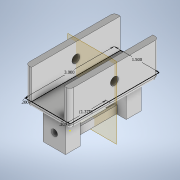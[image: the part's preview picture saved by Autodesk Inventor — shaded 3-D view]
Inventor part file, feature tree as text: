
AUTODESK INVENTOR PART (.ipt)
format: ipt  version: 2020 (Build 240168000, 168)  size: 665,600 bytes
history: native  units: in
note: dims shown in document units (in); Inventor stores cm internally (conversion verified against a paired STEP export)
features: sketch x8, extrude x5, hole x4, fillet x1, plane x1, mirror x1
ambient origin geometry x8: Origin, YZ Plane, XZ Plane, XY Plane, X Axis, Y Axis, Z Axis, Center Point
bodies: Solid1 (feature_tree)
feature tree (20):
  sketch  "Sketch1"  dims[d0=1.5in d1=3.0in]
  extrude  "Extrusion1"  Depth=3.0in
  extrude  "Extrusion2"  Depth=0.2in
  hole  "Hole1"  [1 undecoded]
  extrude  "Extrusion3"  Depth=0.5in
  hole  "Hole2"  [1 undecoded]
  fillet  "Fillet1"  Radius=0.125in
  extrude  "Extrusion4"  Depth=1.0in TaperAngle=0.0deg
  extrude  "Extrusion5"  Depth=0.15in
  hole  "Hole3"  [1 undecoded]
  hole  "Hole4"  [1 undecoded]
  sketch  "Sketch9"  dims[d23=0.45in d24=0.0669in d25=0.75in d26=0.438in d27=0.25in d28=0.5635in d29=1.0in d30=0.8108in d31=0.125in d32=0.125in d33=0.125in d34=0.5in d35=0.5in d36=90.0deg d37=0.1in d38=0.1in d39=0.125in d40=0.075in d41=0.25in d42=1.6in d43=0.0in d44=0.05in d45=0.0in d46=0.5in d47=0.5in d48=0.5in d49=0.375in d50=0.5in d51=0.5in d52=0.213in d53=0.75in d54=0.119in d55=0.25in d56=0.5635in d57=0.25in d58=0.0in d59=0.176in d60=0.75in d61=0.119in d62=0.25in d63=0.5635in d64=0.15in d65=0.0in d66=1.375in]
  plane  "Work Plane1"
  mirror  "Mirror1"
  sketch  "Sketch2"  dims[d2=0.2in d3=0.2in]
  sketch  "Sketch3"  dims[d4=1.0in d5=0.0in d6=0.2in d7=0.0in]
  sketch  "Sketch5"  dims[d8=0.5in]
  sketch  "Sketch6"  dims[d9=0.266in d10=0.75in d11=0.438in d12=0.25in d13=0.5635in d14=1.0in d15=0.8108in d16=0.5in]
  sketch  "Sketch7"  dims[d17=1.0in d18=0.75in d19=0.125in]
  sketch  "Sketch8"  dims[d20=0.125in d21=1.0in d22=0.0in]
note: 4 required parameter values undecoded (feature->parameter linkage not recoverable at this tier; creation-order binding heuristic only, values carry confidence <= 0.55)
